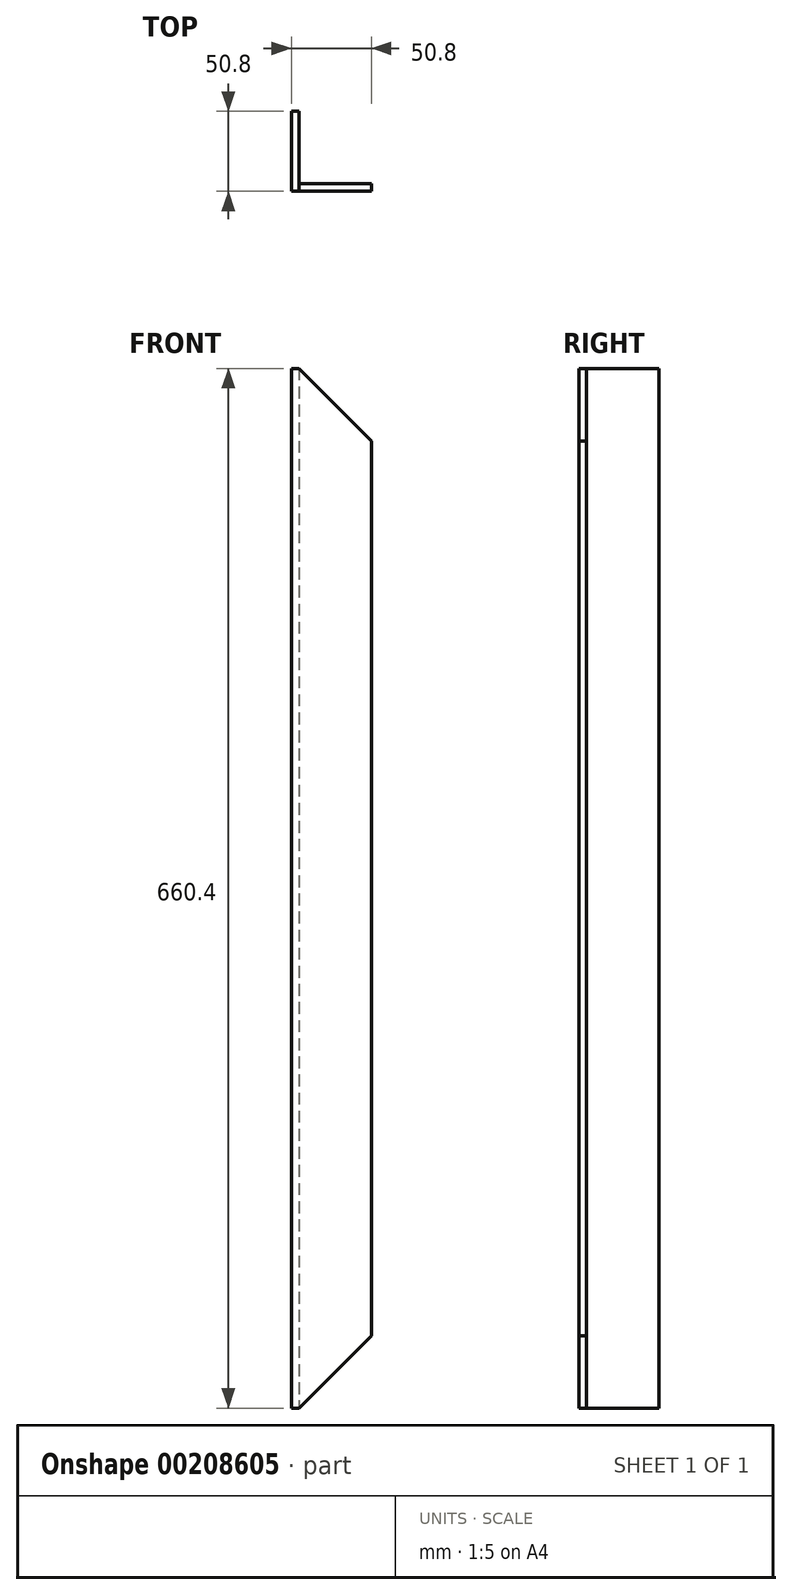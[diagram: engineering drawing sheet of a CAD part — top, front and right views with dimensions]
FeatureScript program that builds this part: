
annotation { "Feature Type Name" : "Feature", "Feature Type Description" : "" }
export const myFeature = defineFeature(function(context is Context, id is Id, definition is map)
    precondition{}
    {
        {
            var Q0;
            Q0=qCreatedBy(makeId("Top.planeOp"),FACE);
            var sketch = newSketch(context, id + "F0", { "sketchPlane" : qUnion([Q0])});
            skLineSegment(sketch, "E0", {"start": v(0, 0) * mm, "end": v(0, 50.8) * mm});
            skLineSegment(sketch, "E1", {"start": v(0, 0) * mm, "end": v(50.8, 0) * mm});
            skLineSegment(sketch, "E2.0", {"start": v(4.76, 4.76) * mm, "end": v(4.76, 50.8) * mm});
            skLineSegment(sketch, "E2.1", {"start": v(4.76, 4.76) * mm, "end": v(50.8, 4.76) * mm});
            skLineSegment(sketch, "E3", {"start": v(0, 50.8) * mm, "end": v(4.76, 50.8) * mm});
            skLineSegment(sketch, "E4", {"start": v(50.8, 4.76) * mm, "end": v(50.8, 0) * mm});
            skSolve(sketch);
        }
        {
            var Q0;
            Q0 = qSketchRegion(id + "F0", true);
            extrude(context, id + "F1", {"entities" : qUnion([Q0]), "endBound" : BoundingType.SYMMETRIC, "depth" : 660.4 * mm});
        }
        {
            var Q0;
            Q0=makeQuery(id+"F1.opExtrude","SWEPT_FACE",FACE,{"disambiguationData":[OSD([sQuery(id+"F0.wireOp",EDGE,"E2.1")])]});
            var sketch = newSketch(context, id + "F2", { "sketchPlane" : qUnion([Q0])});
            skLineSegment(sketch, "E5", {"start": v(-4.76, 330.2) * mm, "end": v(-50.8, 284.16) * mm});
            skLineSegment(sketch, "E6", {"start": v(-50.8, 284.16) * mm, "end": v(-50.8, 330.2) * mm});
            skLineSegment(sketch, "E7", {"start": v(-50.8, 330.2) * mm, "end": v(-4.76, 330.2) * mm});
            skLineSegment(sketch, "E8.MirrorCS", {"start": v(-4.76, -330.2) * mm, "end": v(-50.8, -284.16) * mm});
            skLineSegment(sketch, "E9.MirrorCS", {"start": v(-50.8, -284.16) * mm, "end": v(-50.8, -330.2) * mm});
            skLineSegment(sketch, "E10.MirrorCS", {"start": v(-50.8, -330.2) * mm, "end": v(-4.76, -330.2) * mm});
            skSolve(sketch);
        }
        {
            var Q0;
            Q0 = qSketchRegion(id + "F2", true);
            var Q1;
            Q1=makeQuery(id+"F1.opExtrude","SWEPT_FACE",FACE,{"disambiguationData":[OSD([sQuery(id+"F0.wireOp",EDGE,"E1")])]});
            extrude(context, id + "F3", {"entities" : qUnion([Q0]), "operationType" : NewBodyOperationType.REMOVE, "endBound" : BoundingType.UP_TO_SURFACE, "oppositeDirection" : true, "endBoundEntityFace" : qUnion([Q1]), "depth" : 25.4 * mm});
        }
    });
